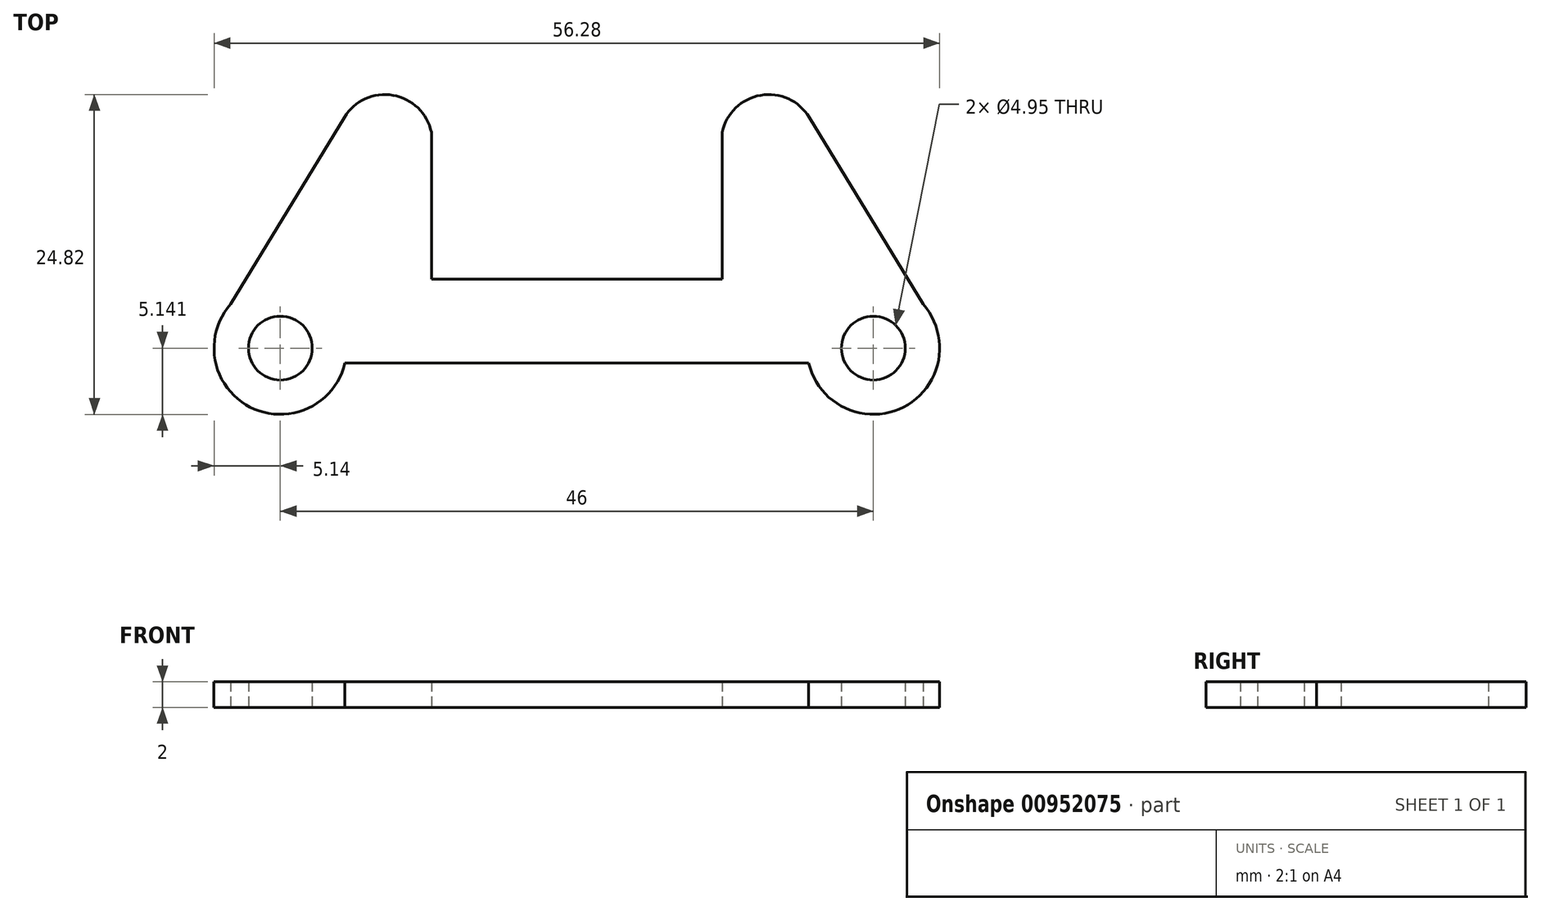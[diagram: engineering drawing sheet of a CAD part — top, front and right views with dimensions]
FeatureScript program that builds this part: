
annotation { "Feature Type Name" : "Feature", "Feature Type Description" : "" }
export const myFeature = defineFeature(function(context is Context, id is Id, definition is map)
    precondition{}
    {
        {
            var Q0;
            Q0=qCreatedBy(makeId("Top.planeOp"),FACE);
            var sketch = newSketch(context, id + "F0", { "sketchPlane" : qUnion([Q0])});
            skCircle(sketch, "E0", {"center": v(-23, -12.9) * mm, "radius": 2.48 * mm});
            skCircle(sketch, "E1", {"center": v(-15, 3.54) * mm, "radius": 1.5 * mm, "construction": true});
            skLineSegment(sketch, "E2", {"start": v(-18.03, 5) * mm, "end": v(-26.85, -9.5) * mm});
            skLineSegment(sketch, "E3", {"start": v(-11.28, 3.84) * mm, "end": v(-11.28, -7.57) * mm});
            skLineSegment(sketch, "E4", {"start": v(-11.28, -7.57) * mm, "end": v(0, -7.57) * mm});
            skLineSegment(sketch, "E5.MirrorCS", {"start": v(11.28, -7.57) * mm, "end": v(0, -7.57) * mm});
            skLineSegment(sketch, "E6.MirrorCS", {"start": v(11.28, 3.84) * mm, "end": v(11.28, -7.57) * mm});
            skLineSegment(sketch, "E7.MirrorCS", {"start": v(18.03, 5) * mm, "end": v(27.8, -11.05) * mm});
            skCircle(sketch, "E8.MirrorC", {"center": v(23, -12.9) * mm, "radius": 2.48 * mm});
            skArc(sketch, "E9", {"start": v(-18.03, 5) * mm, "mid": v(-14.26, 6.71) * mm, "end": v(-11.28, 3.84) * mm});
            skArc(sketch, "E10.MirrorCS", {"start": v(18.03, 5) * mm, "mid": v(14.26, 6.71) * mm, "end": v(11.28, 3.84) * mm});
            skArc(sketch, "E11", {"start": v(-26.85, -9.5) * mm, "mid": v(-25.36, -17.48) * mm, "end": v(-18, -14.07) * mm});
            skLineSegment(sketch, "E12", {"start": v(0, -14.07) * mm, "end": v(-18, -14.07) * mm});
            skLineSegment(sketch, "E13.MirrorCS", {"start": v(0, -14.07) * mm, "end": v(18, -14.07) * mm});
            skPoint(sketch, "E14.orphan", {"position": v(-27.8, -11.05) * mm});
            skArc(sketch, "E15.MirrorCS", {"start": v(26.85, -9.5) * mm, "mid": v(25.36, -17.48) * mm, "end": v(18, -14.07) * mm});
            skCircle(sketch, "E16.MirrorC", {"center": v(15, 3.54) * mm, "radius": 1.5 * mm, "construction": true});
            skSolve(sketch);
        }
        {
            var Q0;
            Q0 = qSketchRegion(id + "F0", true);
            extrude(context, id + "F1", {"entities" : qUnion([Q0]), "depth" : 2 * mm, "offsetDistance" : 25 * mm});
        }
    });
